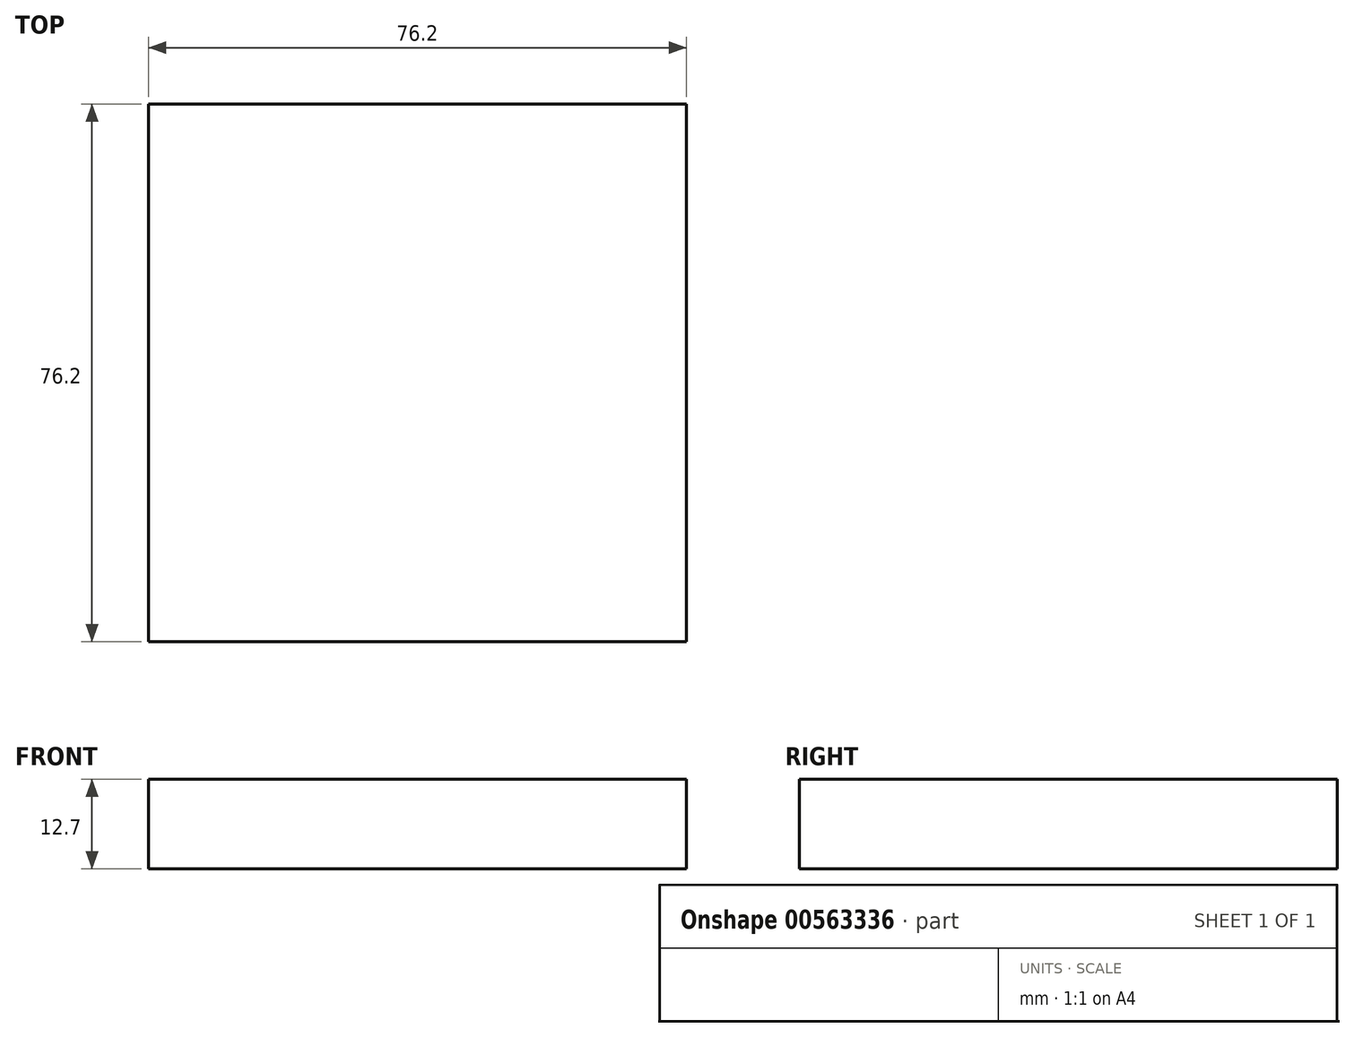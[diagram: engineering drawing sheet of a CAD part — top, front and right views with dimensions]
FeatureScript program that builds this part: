
annotation { "Feature Type Name" : "Feature", "Feature Type Description" : "" }
export const myFeature = defineFeature(function(context is Context, id is Id, definition is map)
    precondition{}
    {
        {
            var Q0;
            Q0=qCreatedBy(makeId("Front.planeOp"),FACE);
            var sketch = newSketch(context, id + "F0", { "sketchPlane" : qUnion([Q0])});
            skLineSegment(sketch, "E0.bottom", {"start": v(-38.1, 6.35) * mm, "end": v(38.1, 6.35) * mm});
            skLineSegment(sketch, "E0.top", {"start": v(-38.1, -6.35) * mm, "end": v(38.1, -6.35) * mm});
            skLineSegment(sketch, "E0.left", {"start": v(-38.1, 6.35) * mm, "end": v(-38.1, -6.35) * mm});
            skLineSegment(sketch, "E0.right", {"start": v(38.1, 6.35) * mm, "end": v(38.1, -6.35) * mm});
            skPoint(sketch, "E0.middle", {"position": v(0, 0) * mm});
            skSolve(sketch);
        }
        {
            var Q0;
            Q0 = qSketchRegion(id + "F0", true);
            extrude(context, id + "F1", {"entities" : qUnion([Q0]), "depth" : 76.2 * mm, "offsetDistance" : 25.4 * mm});
        }
    });
